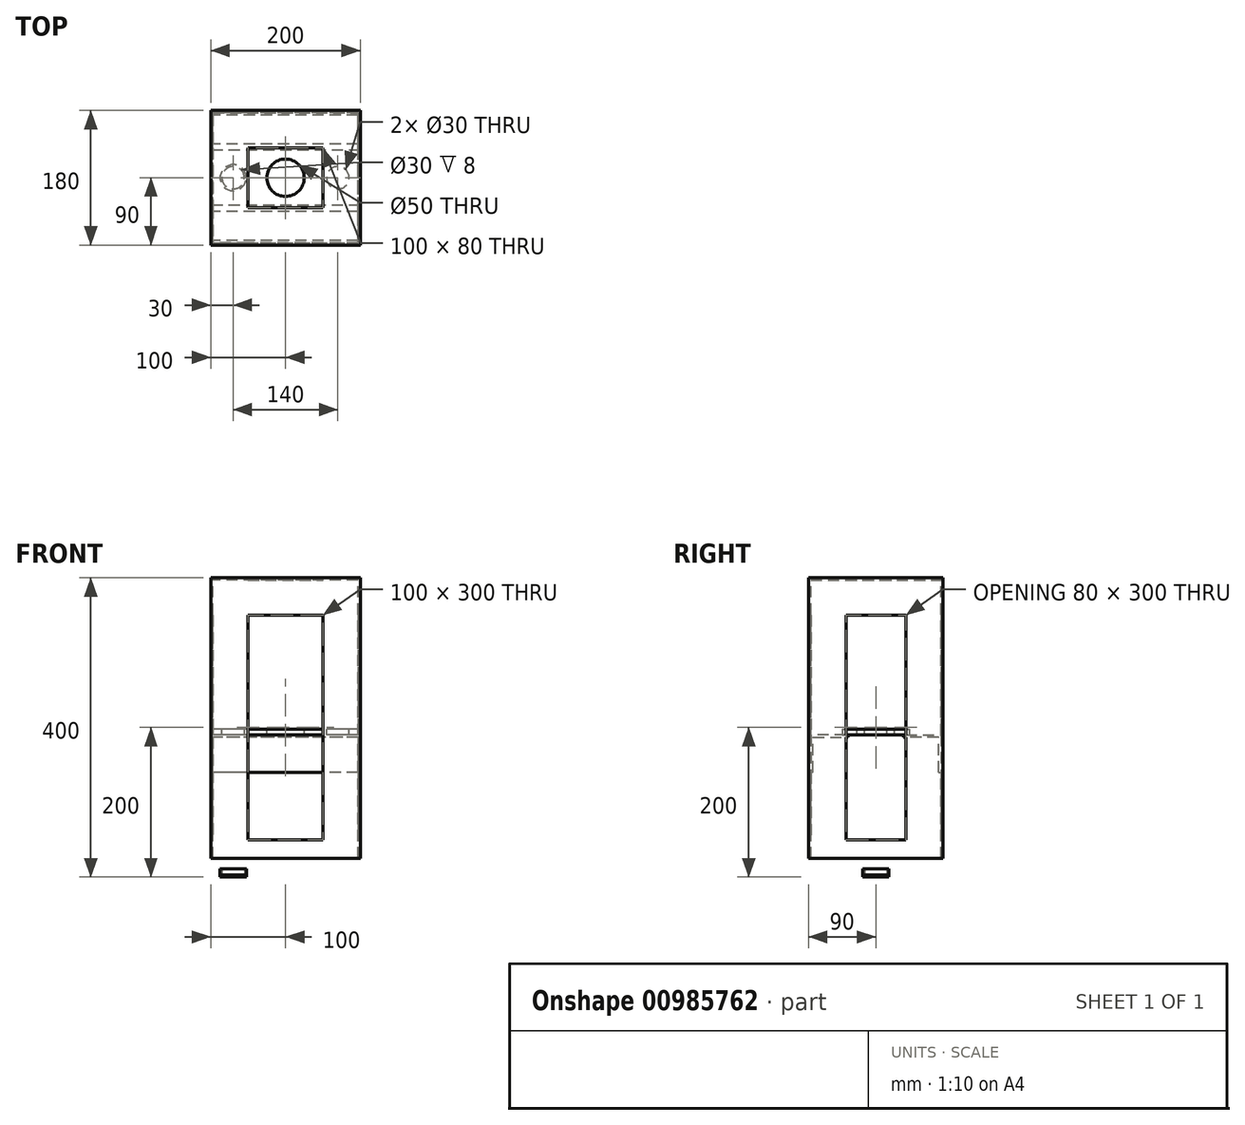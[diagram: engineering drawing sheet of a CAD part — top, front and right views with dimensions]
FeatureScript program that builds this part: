
annotation { "Feature Type Name" : "Feature", "Feature Type Description" : "" }
export const myFeature = defineFeature(function(context is Context, id is Id, definition is map)
    precondition{}
    {
        {
            var Q0;
            Q0=qCreatedBy(makeId("Top.planeOp"),FACE);
            var sketch = newSketch(context, id + "F0", { "sketchPlane" : qUnion([Q0])});
            skLineSegment(sketch, "E0.bottom", {"start": v(97, 45) * mm, "end": v(-97, 45) * mm});
            skLineSegment(sketch, "E0.top", {"start": v(97, -45) * mm, "end": v(-97, -45) * mm});
            skLineSegment(sketch, "E0.left", {"start": v(97, 45) * mm, "end": v(97, -45) * mm});
            skLineSegment(sketch, "E0.right", {"start": v(-97, 45) * mm, "end": v(-97, -45) * mm});
            skPoint(sketch, "E0.middle", {"position": v(0, 0) * mm});
            skCircle(sketch, "E1", {"center": v(0, 0) * mm, "radius": 25 * mm});
            skCircle(sketch, "E2", {"center": v(-70, 0) * mm, "radius": 15 * mm});
            skCircle(sketch, "E3.MirrorC", {"center": v(70, 0) * mm, "radius": 15 * mm});
            skSolve(sketch);
        }
        {
            var Q0;
            Q0=makeQuery(id+"F0.imprint","IMPRINT",FACE,{"disambiguationData":[TD([[makeQuery(id+"F0.imprint","IMPRINT",EDGE,{"derivedFrom":sQuery(id+"F0.wireOp",EDGE,"E0.bottom")}),1.0]])]});
            extrude(context, id + "F1", {"entities" : qUnion([Q0]), "depth" : 8 * mm, "offsetDistance" : 25 * mm});
        }
        {
            var Q0;
            Q0=makeQuery(id+"F1.opExtrude","CAP_FACE",FACE,{"disambiguationData":[OSD([sQuery(id+"F0.wireOp",EDGE,"E0.bottom"),sQuery(id+"F0.wireOp",EDGE,"E0.top"),sQuery(id+"F0.wireOp",EDGE,"E0.left"),sQuery(id+"F0.wireOp",EDGE,"E0.right"),sQuery(id+"F0.wireOp",EDGE,"E1"),sQuery(id+"F0.wireOp",EDGE,"E2"),sQuery(id+"F0.wireOp",EDGE,"E3.MirrorC")])],"isStart":false});
            var sketch = newSketch(context, id + "F2", { "sketchPlane" : qUnion([Q0])});
            skLineSegment(sketch, "E4.bottom", {"start": v(40, 35) * mm, "end": v(-40, 35) * mm});
            skLineSegment(sketch, "E4.top", {"start": v(40, -35) * mm, "end": v(-40, -35) * mm});
            skLineSegment(sketch, "E4.left", {"start": v(40, 35) * mm, "end": v(40, -35) * mm});
            skLineSegment(sketch, "E4.right", {"start": v(-40, 35) * mm, "end": v(-40, -35) * mm});
            skPoint(sketch, "E4.middle", {"position": v(0, 0) * mm});
            skSolve(sketch);
        }
        {
            var Q0;
            Q0 = qSketchRegion(id + "F2", true);
            extrude(context, id + "F3", {"entities" : qUnion([Q0]), "depth" : 3 * mm, "offsetDistance" : 25 * mm});
        }
        {
            var Q0;
            Q0=makeQuery(id+"F3.opExtrude","CAP_FACE",FACE,{"disambiguationData":[OSD([sQuery(id+"F2.wireOp",EDGE,"E4.bottom"),sQuery(id+"F2.wireOp",EDGE,"E4.top"),sQuery(id+"F2.wireOp",EDGE,"E4.left"),sQuery(id+"F2.wireOp",EDGE,"E4.right")])],"isStart":false});
            var sketch = newSketch(context, id + "F4", { "sketchPlane" : qUnion([Q0])});
            skCircle(sketch, "E5", {"center": v(0, 0) * mm, "radius": 14 * mm});
            skSolve(sketch);
        }
        {
            var Q0;
            Q0 = qSketchRegion(id + "F4", true);
            extrude(context, id + "F5", {"entities" : qUnion([Q0]), "operationType" : NewBodyOperationType.REMOVE, "oppositeDirection" : true, "depth" : 25 * mm, "offsetDistance" : 25 * mm});
        }
        {
            var Q0;
            Q0=qCreatedBy(makeId("Front.planeOp"),FACE);
            var sketch = newSketch(context, id + "F6", { "sketchPlane" : qUnion([Q0])});
            skLineSegment(sketch, "E6.bottom", {"start": v(100, -3) * mm, "end": v(-100, -3) * mm});
            skLineSegment(sketch, "E6.top", {"start": v(100, 397) * mm, "end": v(-100, 397) * mm});
            skLineSegment(sketch, "E6.left", {"start": v(100, -3) * mm, "end": v(100, 397) * mm});
            skLineSegment(sketch, "E6.right", {"start": v(-100, -3) * mm, "end": v(-100, 397) * mm});
            skPoint(sketch, "E6.middle", {"position": v(0, 197) * mm});
            skSolve(sketch);
        }
        {
            var Q0;
            Q0 = qSketchRegion(id + "F6", true);
            extrude(context, id + "F7", {"entities" : qUnion([Q0]), "endBound" : BoundingType.SYMMETRIC, "depth" : 180 * mm, "offsetDistance" : 25 * mm});
        }
        {
            var Q0;
            Q0=makeQuery(id+"F7.opExtrude","CAP_FACE",FACE,{"disambiguationData":[OSD([sQuery(id+"F6.wireOp",EDGE,"E6.bottom"),sQuery(id+"F6.wireOp",EDGE,"E6.top"),sQuery(id+"F6.wireOp",EDGE,"E6.left"),sQuery(id+"F6.wireOp",EDGE,"E6.right")])],"isStart":false});
            var sketch = newSketch(context, id + "F8", { "sketchPlane" : qUnion([Q0])});
            skLineSegment(sketch, "E7.bottom", {"start": v(50, 347) * mm, "end": v(-50, 347) * mm});
            skLineSegment(sketch, "E7.top", {"start": v(50, 47) * mm, "end": v(-50, 47) * mm});
            skLineSegment(sketch, "E7.left", {"start": v(50, 347) * mm, "end": v(50, 47) * mm});
            skLineSegment(sketch, "E7.right", {"start": v(-50, 347) * mm, "end": v(-50, 47) * mm});
            skPoint(sketch, "E7.middle", {"position": v(0, 197) * mm});
            skSolve(sketch);
        }
        {
            var Q0;
            Q0=makeQuery(id+"F8.imprint","IMPRINT",FACE,{"disambiguationData":[TD([[makeQuery(id+"F8.imprint","IMPRINT",EDGE,{"derivedFrom":sQuery(id+"F8.wireOp",EDGE,"E7.bottom")}),1.0]])]});
            extrude(context, id + "F9", {"entities" : qUnion([Q0]), "operationType" : NewBodyOperationType.REMOVE, "oppositeDirection" : true, "depth" : 266 * mm, "offsetDistance" : 25 * mm});
        }
        {
            var Q0;
            Q0=makeQuery(id+"F9.boolean.opBoolean","COPY",FACE,{"derivedFrom":makeQuery(id+"F9.opExtrude","SWEPT_FACE",FACE,{"disambiguationData":[OSD([sQuery(id+"F8.wireOp",EDGE,"E7.left")])]})});
            var Q1;
            Q1=makeQuery(id+"F9.boolean.opBoolean","COPY",FACE,{"derivedFrom":makeQuery(id+"F9.opExtrude","SWEPT_FACE",FACE,{"disambiguationData":[OSD([sQuery(id+"F8.wireOp",EDGE,"E7.bottom")])]})});
            var Q2;
            Q2=makeQuery(id+"F9.boolean.opBoolean","COPY",FACE,{"derivedFrom":makeQuery(id+"F9.opExtrude","SWEPT_FACE",FACE,{"disambiguationData":[OSD([sQuery(id+"F8.wireOp",EDGE,"E7.right")])]})});
            var Q3;
            Q3=makeQuery(id+"F9.boolean.opBoolean","COPY",FACE,{"derivedFrom":makeQuery(id+"F9.opExtrude","SWEPT_FACE",FACE,{"disambiguationData":[OSD([sQuery(id+"F8.wireOp",EDGE,"E7.top")])]})});
            shell(context, id + "F10", {"entities" : qUnion([Q0, Q1, Q2, Q3]), "thickness" : 3 * mm});
        }
        {
            var Q0;
            Q0=qCreatedBy(makeId("Right.planeOp"),FACE);
            var sketch = newSketch(context, id + "F11", { "sketchPlane" : qUnion([Q0])});
            skLineSegment(sketch, "E8.bottom", {"start": v(40, 347) * mm, "end": v(-40, 347) * mm});
            skLineSegment(sketch, "E8.top", {"start": v(40, 47) * mm, "end": v(-40, 47) * mm});
            skLineSegment(sketch, "E8.left", {"start": v(40, 347) * mm, "end": v(40, 47) * mm});
            skLineSegment(sketch, "E8.right", {"start": v(-40, 347) * mm, "end": v(-40, 47) * mm});
            skPoint(sketch, "E8.middle", {"position": v(0, 197) * mm});
            skSolve(sketch);
        }
        {
            var Q0;
            Q0 = qSketchRegion(id + "F11", true);
            extrude(context, id + "F12", {"entities" : qUnion([Q0]), "operationType" : NewBodyOperationType.REMOVE, "endBound" : BoundingType.SYMMETRIC, "depth" : 324 * mm, "offsetDistance" : 25 * mm});
        }
        {
            var Q0;
            Q0=makeQuery(id+"F7.opExtrude","SWEPT_FACE",FACE,{"disambiguationData":[OSD([sQuery(id+"F6.wireOp",EDGE,"E6.top")])]});
            var sketch = newSketch(context, id + "F13", { "sketchPlane" : qUnion([Q0])});
            skLineSegment(sketch, "E9.bottom", {"start": v(50, 40) * mm, "end": v(-50, 40) * mm});
            skLineSegment(sketch, "E9.top", {"start": v(50, -40) * mm, "end": v(-50, -40) * mm});
            skLineSegment(sketch, "E9.left", {"start": v(50, 40) * mm, "end": v(50, -40) * mm});
            skLineSegment(sketch, "E9.right", {"start": v(-50, 40) * mm, "end": v(-50, -40) * mm});
            skPoint(sketch, "E9.middle", {"position": v(0, 0) * mm});
            skSolve(sketch);
        }
        {
            var Q0;
            Q0 = qSketchRegion(id + "F13", true);
            extrude(context, id + "F14", {"entities" : qUnion([Q0]), "operationType" : NewBodyOperationType.REMOVE, "oppositeDirection" : true, "depth" : 517 * mm, "offsetDistance" : 25 * mm});
        }
        {
            var Q0;
            Q0=makeQuery(id+"F7.opExtrude","SWEPT_FACE",FACE,{"disambiguationData":[OSD([sQuery(id+"F6.wireOp",EDGE,"E6.bottom")])]});
            var sketch = newSketch(context, id + "F15", { "sketchPlane" : qUnion([Q0])});
            skCircle(sketch, "E10", {"center": v(70, 0) * mm, "radius": 17.5 * mm});
            skCircle(sketch, "E11.MirrorC", {"center": v(-70, 0) * mm, "radius": 17.5 * mm});
            skSolve(sketch);
        }
        {
            var Q0;
            Q0=makeQuery(id+"F15.imprint","IMPRINT",FACE,{"disambiguationData":[TD([[makeQuery(id+"F15.imprint","IMPRINT",EDGE,{"derivedFrom":sQuery(id+"F15.wireOp",EDGE,"E10")}),1.0]])]});
            var Q1;
            Q1=makeQuery(id+"F15.imprint","IMPRINT",FACE,{"disambiguationData":[TD([[makeQuery(id+"F15.imprint","IMPRINT",EDGE,{"derivedFrom":sQuery(id+"F15.wireOp",EDGE,"E11.MirrorC")}),-1.0]])]});
            extrude(context, id + "F16", {"entities" : qUnion([Q0, Q1]), "operationType" : NewBodyOperationType.REMOVE, "oppositeDirection" : true, "depth" : 25 * mm, "offsetDistance" : 25 * mm});
        }
        {
            var Q0;
            Q0=qCreatedBy(makeId("Right.planeOp"),FACE);
            var sketch = newSketch(context, id + "F17", { "sketchPlane" : qUnion([Q0])});
            skLineSegment(sketch, "E12.bottom", {"start": v(84, 137) * mm, "end": v(87, 137) * mm});
            skLineSegment(sketch, "E12.top", {"start": v(37, 187) * mm, "end": v(87, 187) * mm});
            skLineSegment(sketch, "E12.left", {"start": v(37, 184) * mm, "end": v(37, 187) * mm});
            skLineSegment(sketch, "E12.right", {"start": v(87, 137) * mm, "end": v(87, 187) * mm});
            skPoint(sketch, "E12.middle", {"position": v(62, 162) * mm});
            skLineSegment(sketch, "E13", {"start": v(84, 137) * mm, "end": v(84, 184) * mm});
            skLineSegment(sketch, "E14", {"start": v(84, 184) * mm, "end": v(37, 184) * mm});
            skPoint(sketch, "E15.orphan", {"position": v(37, 137) * mm});
            skLineSegment(sketch, "E16.MirrorCS", {"start": v(-84, 137) * mm, "end": v(-87, 137) * mm});
            skLineSegment(sketch, "E17.MirrorCS", {"start": v(-37, 184) * mm, "end": v(-37, 187) * mm});
            skLineSegment(sketch, "E18.MirrorCS", {"start": v(-37, 187) * mm, "end": v(-87, 187) * mm});
            skLineSegment(sketch, "E19.MirrorCS", {"start": v(-84, 184) * mm, "end": v(-37, 184) * mm});
            skPoint(sketch, "E20.MirrorP", {"position": v(-62, 162) * mm});
            skLineSegment(sketch, "E21.MirrorCS", {"start": v(-87, 137) * mm, "end": v(-87, 187) * mm});
            skLineSegment(sketch, "E22.MirrorCS", {"start": v(-84, 137) * mm, "end": v(-84, 184) * mm});
            skPoint(sketch, "E23.MirrorP", {"position": v(-37, 137) * mm});
            skSolve(sketch);
        }
        {
            var Q0;
            Q0 = qSketchRegion(id + "F17", true);
            extrude(context, id + "F18", {"entities" : qUnion([Q0]), "operationType" : NewBodyOperationType.ADD, "endBound" : BoundingType.SYMMETRIC, "depth" : 200 * mm, "offsetDistance" : 25 * mm});
        }
        {
            var Q0;
            Q0=makeQuery(id+"F18.opExtrude","SWEPT_FACE",FACE,{"disambiguationData":[OSD([sQuery(id+"F17.wireOp",EDGE,"E12.top")])]});
            var sketch = newSketch(context, id + "F19", { "sketchPlane" : qUnion([Q0])});
            skLineSegment(sketch, "E24.bottom", {"start": v(97, -45) * mm, "end": v(-97, -45) * mm});
            skLineSegment(sketch, "E24.top", {"start": v(97, 45) * mm, "end": v(-97, 45) * mm});
            skLineSegment(sketch, "E24.left", {"start": v(97, -45) * mm, "end": v(97, 45) * mm});
            skLineSegment(sketch, "E24.right", {"start": v(-97, -45) * mm, "end": v(-97, 45) * mm});
            skPoint(sketch, "E24.middle", {"position": v(0, 0) * mm});
            skSolve(sketch);
        }
        {
            var Q0;
            Q0 = qSketchRegion(id + "F19", true);
            extrude(context, id + "F20", {"entities" : qUnion([Q0]), "depth" : 8 * mm, "offsetDistance" : 25 * mm});
        }
        {
            var Q0;
            Q0=makeQuery(id+"F20.opExtrude","CAP_FACE",FACE,{"disambiguationData":[OSD([sQuery(id+"F19.wireOp",EDGE,"E24.bottom"),sQuery(id+"F19.wireOp",EDGE,"E24.top"),sQuery(id+"F19.wireOp",EDGE,"E24.left"),sQuery(id+"F19.wireOp",EDGE,"E24.right")])],"isStart":false});
            var sketch = newSketch(context, id + "F21", { "sketchPlane" : qUnion([Q0])});
            skCircle(sketch, "E25", {"center": v(0, 0) * mm, "radius": 25 * mm});
            skCircle(sketch, "E26", {"center": v(70, 0) * mm, "radius": 15 * mm});
            skCircle(sketch, "E27.MirrorC", {"center": v(-70, 0) * mm, "radius": 15 * mm});
            skSolve(sketch);
        }
        {
            var Q0;
            Q0 = qSketchRegion(id + "F21", true);
            extrude(context, id + "F22", {"entities" : qUnion([Q0]), "operationType" : NewBodyOperationType.REMOVE, "oppositeDirection" : true, "depth" : 25 * mm, "offsetDistance" : 25 * mm});
        }
    });
